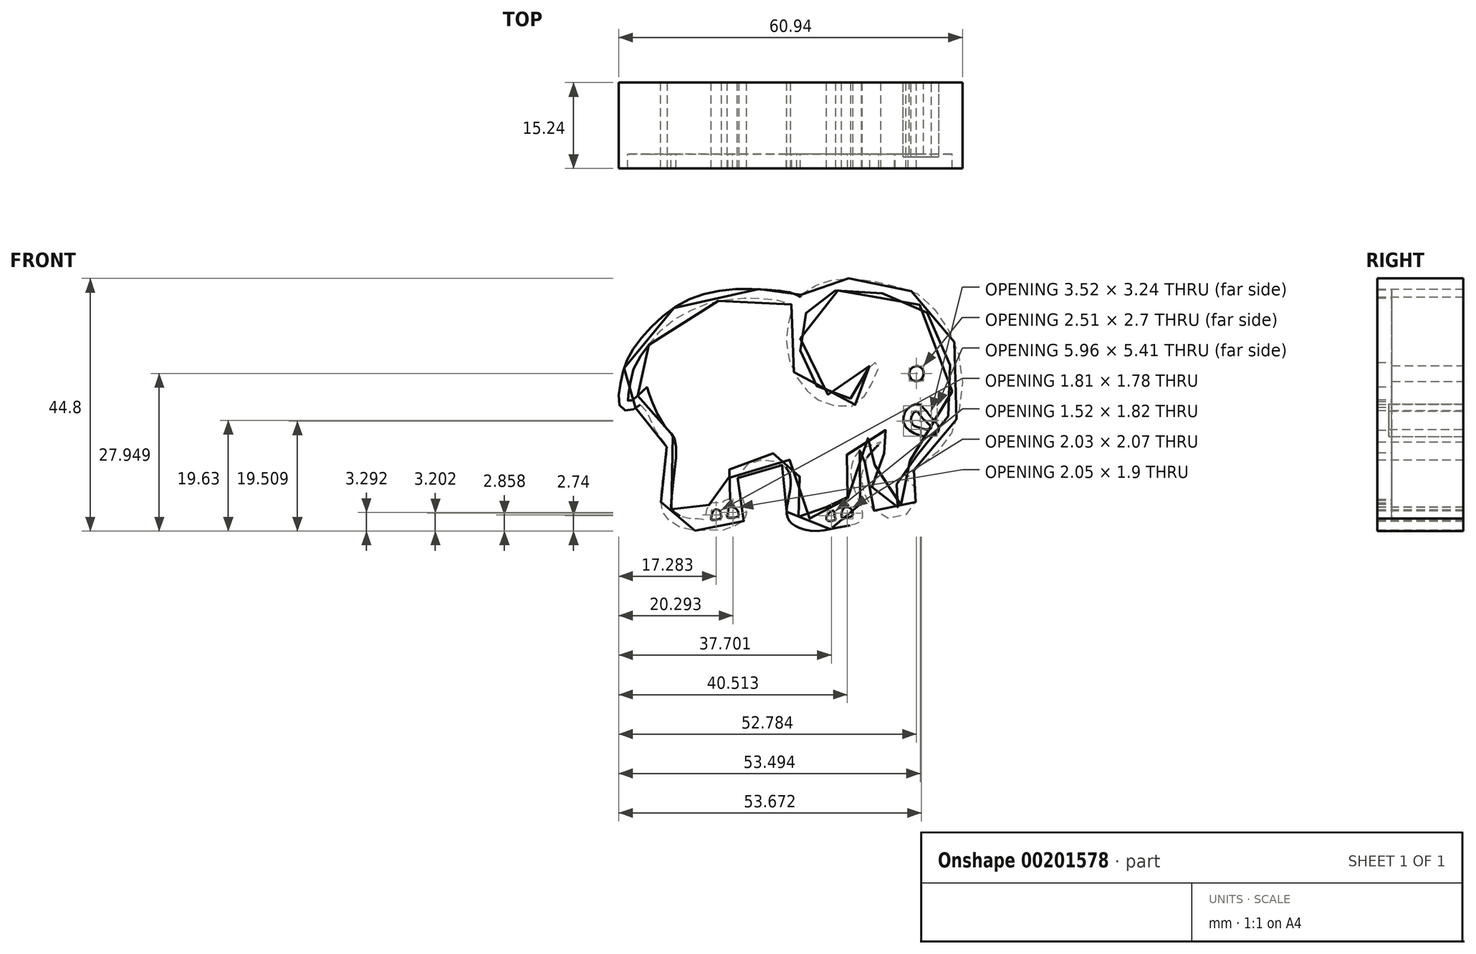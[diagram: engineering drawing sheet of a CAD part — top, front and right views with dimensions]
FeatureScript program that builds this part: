
annotation { "Feature Type Name" : "Feature", "Feature Type Description" : "" }
export const myFeature = defineFeature(function(context is Context, id is Id, definition is map)
    precondition{}
    {
        {
            var Q0;
            Q0=qCreatedBy(makeId("Front.planeOp"),FACE);
            var sketch = newSketch(context, id + "F0", { "sketchPlane" : qUnion([Q0])});
            skLineSegment(sketch, "E0", {"start": v(-454.87, 153.52) * mm, "end": v(-391.37, 153.52) * mm});
            skLineSegment(sketch, "E1", {"start": v(-454.87, 153.52) * mm, "end": v(-454.87, 102.72) * mm});
            skFitSpline(sketch, "E2", {"points": [v(-17.15, 22.5) * mm, v(-14.9, 24) * mm, v(-12.4, 25) * mm, v(-9.06, 25.42) * mm, v(-4.3, 24.92) * mm, v(0, 23.92) * mm, v(4.12, 22.34) * mm, v(7.37, 18.75) * mm, v(10.29, 13.5) * mm, v(11.45, 6.4) * mm, v(10.29, 0) * mm, v(7.95, -4.44) * mm, v(3.7, -8.02) * mm, v(1.61, -9.77) * mm, v(1.53, -10.52) * mm, v(2.78, -11.36) * mm, v(3.28, -13.11) * mm, v(2.61, -15.45) * mm, v(0, -17.03) * mm, v(-2.64, -16.86) * mm, v(-4.98, -14.78) * mm, v(-6.23, -11.7) * mm, v(-6.4, -9.1) * mm, v(-5.14, -5.94) * mm, v(-2.97, -3.6) * mm, v(-3.73, -3.85) * mm, v(-6.4, -4.84) * mm, v(-7.9, -6.77) * mm, v(-8.23, -10.2) * mm, v(-6.64, -14.7) * mm, v(-6.31, -16.86) * mm, v(-6.9, -17.86) * mm, v(-9.4, -18.53) * mm, v(-15.15, -19.37) * mm, v(-18.49, -18.28) * mm, v(-19.49, -17.11) * mm, v(-19.66, -15.2) * mm, v(-19.16, -12.53) * mm, v(-19.24, -9.02) * mm, v(-20.74, -7.52) * mm, v(-23.16, -6.77) * mm, v(-26.83, -7.69) * mm, v(-28.41, -10.27) * mm, v(-27.91, -12.6) * mm, v(-26.91, -15.61) * mm, v(-26.91, -17.2) * mm, v(-28.08, -18.03) * mm, v(-30.58, -19.2) * mm, v(-33, -19.2) * mm, v(-37.17, -19.2) * mm, v(-40, -17.86) * mm, v(-41.42, -16.53) * mm, v(-42, -14.2) * mm, v(-41.67, -10.02) * mm, v(-41, -6.19) * mm, v(-41, -4.35) * mm, v(-43.26, -1.02) * mm, v(-45.34, 3.07) * mm, v(-46.85, 2.24) * mm, v(-49.01, 2.4) * mm, v(-49.35, 5.66) * mm, v(-48.18, 10.5) * mm, v(-44.84, 15.58) * mm, v(-38.25, 21.09) * mm, v(-30.25, 23.42) * mm, v(-21.82, 23.34) * mm, v(-18.63, 22.82) * mm, v(-17.48, 22.26) * mm, v(-17.28, 22.17) * mm, v(-17.25, 22.3) * mm, v(-17.15, 22.5) * mm]});
            skPoint(sketch, "E3.76.internal.snap0", {"position": v(-122.14, -3.6) * mm});
            skFitSpline(sketch, "E3", {"points": [v(-44.13, 13.62) * mm, v(-42.07, 16.13) * mm, v(-39.84, 18.01) * mm, v(-36.6, 19.8) * mm, v(-33.3, 21.11) * mm, v(-29.8, 21.7) * mm, v(-26.9, 21.98) * mm, v(-24.47, 21.9) * mm, v(-21.27, 21.56) * mm, v(-19.14, 20.96) * mm, v(-18.84, 20.8) * mm, v(-18.83, 20.15) * mm, v(-19.08, 19.01) * mm, v(-19.45, 17.2) * mm, v(-19.78, 15.05) * mm, v(-19.4, 11.54) * mm, v(-17.89, 7.86) * mm, v(-16.2, 5.65) * mm, v(-14.56, 4.14) * mm, v(-12.34, 3.2) * mm, v(-9.28, 2.6) * mm, v(-6.77, 3.55) * mm, v(-5.36, 5.53) * mm, v(-4.53, 6.89) * mm, v(-3.47, 9.48) * mm, v(-3.53, 10.42) * mm, v(-4.03, 10.54) * mm, v(-4.77, 10.3) * mm, v(-5.33, 8.98) * mm, v(-5.92, 7.06) * mm, v(-6.86, 5.44) * mm, v(-7.98, 4.35) * mm, v(-9.75, 3.9) * mm, v(-11.58, 4.44) * mm, v(-13.32, 5.44) * mm, v(-14.9, 6.86) * mm, v(-16.6, 9.19) * mm, v(-17.15, 11.43) * mm, v(-17.28, 12.78) * mm, v(-17.28, 14.58) * mm, v(-16.94, 16.47) * mm, v(-16.35, 18.95) * mm, v(-15.76, 20.36) * mm, v(-14.82, 21.36) * mm, v(-12.5, 22.9) * mm, v(-9.9, 23.37) * mm, v(-6.83, 23.4) * mm, v(-3.73, 22.93) * mm, v(0.3, 22.17) * mm, v(3.37, 21.1) * mm, v(5.7, 18.62) * mm, v(8.27, 13.79) * mm, v(9.3, 10.04) * mm, v(9.62, 5.91) * mm, v(9.36, 2.4) * mm, v(8.27, -0.58) * mm, v(6.41, -3.44) * mm, v(3.4, -5.94) * mm, v(1.2, -7.8) * mm, v(0, -9.19) * mm, v(-0.4, -10.63) * mm, v(0.54, -11.81) * mm, v(1.57, -12.34) * mm, v(1.81, -13.5) * mm, v(0.57, -14.76) * mm, v(-1.55, -15.64) * mm, v(-2.76, -14.73) * mm, v(-4.06, -12.78) * mm, v(-4.8, -10.8) * mm, v(-4.82, -8.95) * mm, v(-3.7, -7.18) * mm, v(-2.23, -5.44) * mm, v(-0.78, -3.58) * mm, v(-0.58, -2.4) * mm, v(-0.96, -1.75) * mm, v(-2.26, -1.52) * mm, v(-6.4, -3.6) * mm, v(-8.16, -4.84) * mm, v(-9.19, -6.09) * mm, v(-9.75, -8.27) * mm, v(-9.84, -10.72) * mm, v(-8.92, -13.64) * mm, v(-9.34, -13.76) * mm, v(-9.96, -13.87) * mm, v(-10.99, -14.55) * mm, v(-11.72, -14.61) * mm, v(-12.7, -15.17) * mm, v(-13.35, -16.23) * mm, v(-13.82, -17.18) * mm, v(-14.8, -17.27) * mm, v(-17.77, -16.76) * mm, v(-17.92, -16.38) * mm, v(-17.65, -14.23) * mm, v(-17.28, -10.72) * mm, v(-18.06, -7.92) * mm, v(-19.5, -6.53) * mm, v(-20.9, -5.85) * mm, v(-22.78, -5.5) * mm, v(-25.9, -5.66) * mm, v(-29.43, -7.53) * mm, v(-30.09, -10.25) * mm, v(-30.05, -10.78) * mm, v(-29.37, -13.62) * mm, v(-29.3, -13.94) * mm, v(-29.96, -13.75) * mm, v(-30.96, -14.22) * mm, v(-31.21, -14.44) * mm, v(-31.9, -14.4) * mm, v(-33.05, -14.47) * mm, v(-33.74, -15.25) * mm, v(-34.2, -17) * mm, v(-34.33, -17.3) * mm, v(-34.93, -17.25) * mm, v(-36.3, -17.22) * mm, v(-37.52, -17.03) * mm, v(-38.99, -16.5) * mm, v(-40.02, -15.65) * mm, v(-40.18, -15.15) * mm, v(-39.93, -11.69) * mm, v(-39.46, -7.78) * mm, v(-39.3, -4.6) * mm, v(-39.58, -3.06) * mm, v(-40.02, -2.22) * mm, v(-41.74, -0.22) * mm, v(-43.61, 3.72) * mm, v(-44.18, 5.37) * mm, v(-44.55, 6.18) * mm, v(-45.18, 5.53) * mm, v(-46.4, 4.37) * mm, v(-47.14, 3.78) * mm, v(-47.64, 3.6) * mm, v(-47.9, 3.97) * mm, v(-47.74, 5.06) * mm, v(-46.83, 9.4) * mm, v(-44.13, 13.62) * mm]});
            skFitSpline(sketch, "E4", {"points": [v(4.1, 9.54) * mm, v(3.56, 9.91) * mm, v(2.91, 9.8) * mm, v(2.34, 9.4) * mm, v(2.07, 8.82) * mm, v(2.2, 7.78) * mm, v(2.99, 7.22) * mm, v(3.95, 7.33) * mm, v(4.43, 7.86) * mm, v(4.58, 8.57) * mm, v(4.45, 9.2) * mm, v(4.1, 9.54) * mm]});
            skFitSpline(sketch, "E5", {"points": [v(-33.1, -17.27) * mm, v(-33.05, -16.64) * mm, v(-32.84, -16.02) * mm, v(-32.56, -15.68) * mm, v(-32.26, -15.6) * mm, v(-31.81, -15.65) * mm, v(-31.53, -15.85) * mm, v(-31.34, -16.59) * mm, v(-31.28, -16.98) * mm, v(-31.43, -17.15) * mm, v(-31.72, -17.25) * mm, v(-32.14, -17.41) * mm, v(-32.6, -17.41) * mm, v(-33, -17.42) * mm, v(-33.1, -17.27) * mm]});
            skFitSpline(sketch, "E6", {"points": [v(-30.21, -16.95) * mm, v(-30.21, -16.58) * mm, v(-30.07, -15.7) * mm, v(-29.93, -15.14) * mm, v(-29.6, -15.06) * mm, v(-28.87, -15.3) * mm, v(-28.44, -15.73) * mm, v(-28.2, -16.34) * mm, v(-28.18, -16.66) * mm, v(-28.66, -16.92) * mm, v(-29.06, -17.02) * mm, v(-29.73, -17.04) * mm, v(-30.21, -16.95) * mm]});
            skFitSpline(sketch, "E7", {"points": [v(-12.54, -17.48) * mm, v(-12.45, -16.53) * mm, v(-11.76, -15.89) * mm, v(-11.4, -15.74) * mm, v(-11.29, -16) * mm, v(-11.23, -16.58) * mm, v(-11.04, -17.1) * mm, v(-11.02, -17.29) * mm, v(-11.18, -17.45) * mm, v(-12.54, -17.48) * mm]});
            skFitSpline(sketch, "E8", {"points": [v(-9.77, -17.21) * mm, v(-9.97, -16.22) * mm, v(-9.75, -15.61) * mm, v(-9.35, -15.16) * mm, v(-8.4, -15.38) * mm, v(-7.94, -16.39) * mm, v(-8.18, -16.76) * mm, v(-9.27, -17.07) * mm, v(-9.77, -17.21) * mm]});
            skFitSpline(sketch, "E9", {"points": [v(2.35, 2.75) * mm, v(1.35, 1.79) * mm, v(1.03, -0.14) * mm, v(2.31, -1.71) * mm, v(4.81, -2.6) * mm, v(6.78, -2.17) * mm, v(7.3, -1.42) * mm, v(7.04, -0.42) * mm, v(6.17, 0.53) * mm, v(5.2, 1.71) * mm, v(4.4, 2.64) * mm, v(3.6, 3.13) * mm, v(2.35, 2.75) * mm]});
            skFitSpline(sketch, "E10", {"points": [v(3.24, 1.87) * mm, v(2.6, 1.28) * mm, v(2.33, 0.3) * mm, v(2.72, -0.58) * mm, v(3.65, -0.99) * mm, v(5.05, -1.36) * mm, v(5.78, -1.26) * mm, v(5.95, -1.03) * mm, v(5.64, -0.58) * mm, v(4.71, 0.3) * mm, v(3.73, 1.51) * mm, v(3.24, 1.87) * mm]});
            skSolve(sketch);
        }
        {
            var Q0;
            Q0=makeQuery(id+"F0.imprint","IMPRINT",FACE,{"disambiguationData":[TD([[makeQuery(id+"F0.imprint","IMPRINT",EDGE,{"derivedFrom":sQuery(id+"F0.wireOp",EDGE,"E3")}),-1.0]])]});
            var Q1;
            Q1=sQuery(id+"F0.wireOp",EDGE,"E2");
            extrude(context, id + "F1", {"entities" : qUnion([Q0]), "surfaceEntities" : qUnion([Q1]), "depth" : 12.7 * mm});
        }
        {
            var Q0;
            Q0=makeQuery(id+"F0.imprint","IMPRINT",FACE,{"disambiguationData":[TD([[makeQuery(id+"F0.imprint","IMPRINT",EDGE,{"derivedFrom":sQuery(id+"F0.wireOp",EDGE,"E2")}),-1.0]])]});
            extrude(context, id + "F2", {"entities" : qUnion([Q0]), "operationType" : NewBodyOperationType.ADD, "depth" : 15.24 * mm});
        }
        {
            var Q0;
            Q0=makeQuery(id+"F0.imprint","IMPRINT",FACE,{"disambiguationData":[TD([[makeQuery(id+"F0.imprint","IMPRINT",EDGE,{"derivedFrom":sQuery(id+"F0.wireOp",EDGE,"E10")}),1.0]])]});
            extrude(context, id + "F3", {"entities" : qUnion([Q0]), "depth" : 13.2 * mm});
        }
        {
            var Q0;
            Q0=makeQuery(id+"F0.imprint","IMPRINT",FACE,{"disambiguationData":[TD([[makeQuery(id+"F0.imprint","IMPRINT",EDGE,{"derivedFrom":sQuery(id+"F0.wireOp",EDGE,"E9")}),1.0]])]});
            extrude(context, id + "F4", {"entities" : qUnion([Q0]), "depth" : 13.2 * mm});
        }
    });
